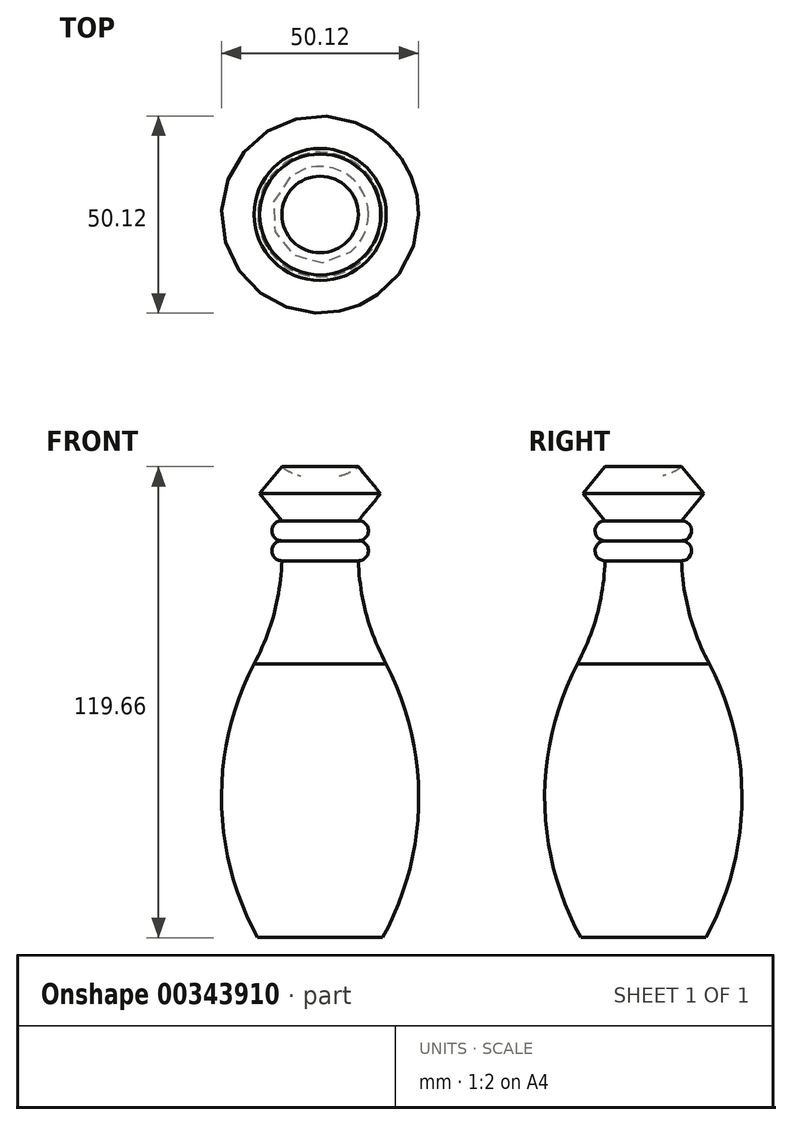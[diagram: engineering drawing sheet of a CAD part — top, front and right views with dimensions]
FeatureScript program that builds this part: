
annotation { "Feature Type Name" : "Feature", "Feature Type Description" : "" }
export const myFeature = defineFeature(function(context is Context, id is Id, definition is map)
    precondition{}
    {
        {
            var Q0;
            Q0=qCreatedBy(makeId("Front.planeOp"),FACE);
            var sketch = newSketch(context, id + "F0", { "sketchPlane" : qUnion([Q0])});
            skLineSegment(sketch, "E0", {"start": v(0, 0) * mm, "end": v(0, -139.65) * mm});
            skArc(sketch, "E1", {"start": v(9.73, -19.99) * mm, "mid": v(12.75, -6.16) * mm, "end": v(0, 0) * mm});
            skLineSegment(sketch, "E2", {"start": v(9.73, -19.99) * mm, "end": v(15.37, -26.86) * mm});
            skLineSegment(sketch, "E3", {"start": v(15.37, -26.86) * mm, "end": v(9.73, -33.74) * mm});
            skArc(sketch, "E4", {"start": v(9.73, -38.82) * mm, "mid": v(12.27, -36.28) * mm, "end": v(9.73, -33.74) * mm});
            skArc(sketch, "E5", {"start": v(9.73, -43.9) * mm, "mid": v(12.27, -41.36) * mm, "end": v(9.73, -38.82) * mm});
            skArc(sketch, "E6", {"start": v(9.73, -43.9) * mm, "mid": v(11.73, -57.42) * mm, "end": v(16.79, -70.13) * mm});
            skLineSegment(sketch, "E7", {"start": v(0, -139.65) * mm, "end": v(15.85, -139.65) * mm});
            skArc(sketch, "E8", {"start": v(15.85, -139.65) * mm, "mid": v(25.05, -105) * mm, "end": v(16.79, -70.13) * mm});
            skSolve(sketch);
        }
        {
            var Q0;
            Q0 = qSketchRegion(id + "F0", true);
            var Q1;
            Q1=sQuery(id+"F0.wireOp",EDGE,"E0");
            revolve(context, id + "F1", {"entities" : qUnion([Q0]), "axis" : qUnion([Q1]), "revolveType" : RevolveType.FULL});
        }
    });
